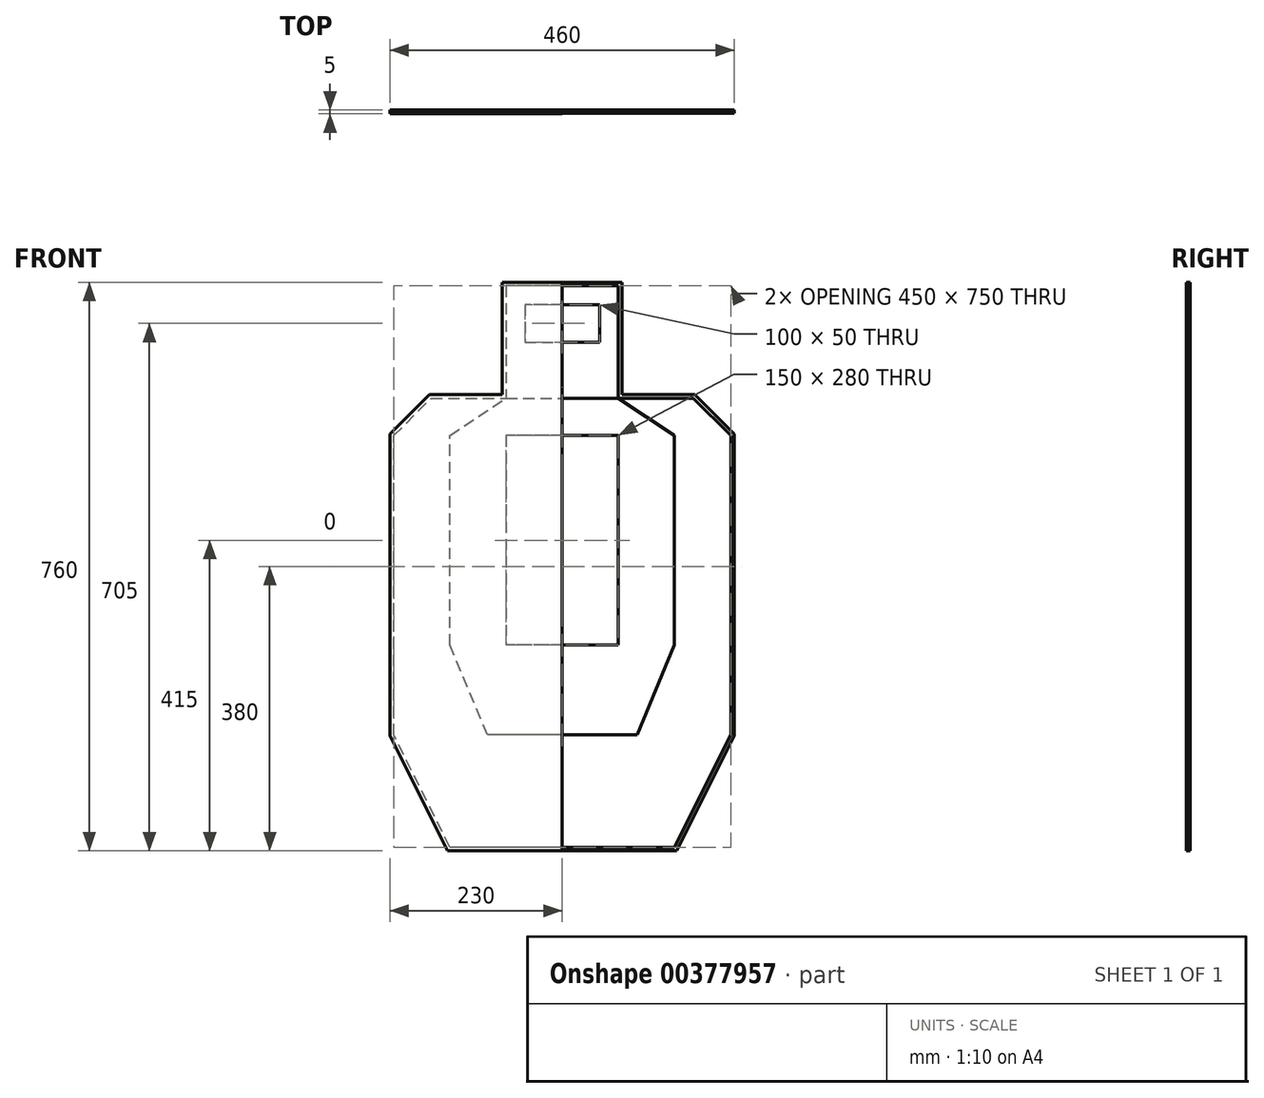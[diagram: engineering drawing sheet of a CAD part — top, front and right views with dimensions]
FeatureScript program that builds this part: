
annotation { "Feature Type Name" : "Feature", "Feature Type Description" : "" }
export const myFeature = defineFeature(function(context is Context, id is Id, definition is map)
    precondition{}
    {
        {
            var Q0;
            Q0=qCreatedBy(makeId("Front.planeOp"),FACE);
            var sketch = newSketch(context, id + "F0", { "sketchPlane" : qUnion([Q0])});
            skLineSegment(sketch, "E0.bottom", {"start": v(0, 100) * mm, "end": v(50, 100) * mm, "construction": true});
            skLineSegment(sketch, "E0.top", {"start": v(0, 125) * mm, "end": v(50, 125) * mm});
            skLineSegment(sketch, "E0.right", {"start": v(50, 100) * mm, "end": v(50, 125) * mm});
            skLineSegment(sketch, "E1.MirrorCS", {"start": v(0, 75) * mm, "end": v(50, 75) * mm});
            skLineSegment(sketch, "E2.MirrorCS", {"start": v(50, 100) * mm, "end": v(50, 75) * mm});
            skLineSegment(sketch, "E3.MirrorCS", {"start": v(0, 0) * mm, "end": v(0, 100) * mm, "construction": true});
            skLineSegment(sketch, "E4.MirrorCS", {"start": v(0, 125) * mm, "end": v(-50, 125) * mm});
            skLineSegment(sketch, "E5.MirrorCS", {"start": v(-50, 100) * mm, "end": v(-50, 125) * mm});
            skLineSegment(sketch, "E6.MirrorCS", {"start": v(-50, 100) * mm, "end": v(-50, 75) * mm});
            skLineSegment(sketch, "E7.MirrorCS", {"start": v(0, 75) * mm, "end": v(-50, 75) * mm});
            skSolve(sketch);
        }
        {
            var Q0;
            Q0=qSketchRegion(id+"F0",true);
            extrude(context, id + "F1", {"entities" : qUnion([Q0]), "oppositeDirection" : true, "depth" : 3 * mm});
        }
        {
            var Q0;
            Q0=qCreatedBy(makeId("Front.planeOp"),FACE);
            var sketch = newSketch(context, id + "F2", { "sketchPlane" : qUnion([Q0])});
            skLineSegment(sketch, "E8", {"start": v(75, 0) * mm, "end": v(75, 150) * mm});
            skLineSegment(sketch, "E9", {"start": v(75, 150) * mm, "end": v(-75, 150) * mm});
            skLineSegment(sketch, "E10", {"start": v(-75, 150) * mm, "end": v(-75, 0) * mm});
            skLineSegment(sketch, "E11", {"start": v(-75, 0) * mm, "end": v(75, 0) * mm});
            skLineSegment(sketch, "E12.0", {"start": v(0, 125) * mm, "end": v(-50, 125) * mm});
            skLineSegment(sketch, "E13.0", {"start": v(0, 125) * mm, "end": v(50, 125) * mm});
            skLineSegment(sketch, "E14.0", {"start": v(50, 100) * mm, "end": v(50, 125) * mm});
            skLineSegment(sketch, "E15.1", {"start": v(50, 100) * mm, "end": v(50, 75) * mm});
            skLineSegment(sketch, "E16.0", {"start": v(0, 75) * mm, "end": v(50, 75) * mm});
            skLineSegment(sketch, "E17.0", {"start": v(0, 75) * mm, "end": v(-50, 75) * mm});
            skLineSegment(sketch, "E18.0", {"start": v(-50, 100) * mm, "end": v(-50, 75) * mm});
            skLineSegment(sketch, "E19.1", {"start": v(-50, 100) * mm, "end": v(-50, 125) * mm});
            skLineSegment(sketch, "E20", {"start": v(0, 125) * mm, "end": v(0, 150) * mm, "construction": true});
            skLineSegment(sketch, "E21", {"start": v(0, 150) * mm, "end": v(0, 137.5) * mm, "construction": true});
            skSolve(sketch);
        }
        {
            var Q0;
            {var subQ0=sQuery(id+"F2.wireOp",EDGE,"E8");Q0=makeQuery(id+"F2.imprint","IMPRINT",FACE,{"disambiguationData":[TD([[makeQuery(id+"F2.imprint","IMPRINT",EDGE,{"derivedFrom":subQ0}),1.0]])]});}
            extrude(context, id + "F3", {"entities" : qUnion([Q0]), "oppositeDirection" : true, "depth" : 3 * mm});
        }
        {
            var Q0;
            Q0=qCreatedBy(makeId("Front.planeOp"),FACE);
            var sketch = newSketch(context, id + "F4", { "sketchPlane" : qUnion([Q0])});
            skLineSegment(sketch, "E22.bottom", {"start": v(75, -50) * mm, "end": v(-75, -50) * mm});
            skLineSegment(sketch, "E22.top", {"start": v(75, -330) * mm, "end": v(-75, -330) * mm});
            skLineSegment(sketch, "E22.left", {"start": v(75, -50) * mm, "end": v(75, -330) * mm});
            skLineSegment(sketch, "E22.right", {"start": v(-75, -50) * mm, "end": v(-75, -330) * mm});
            skLineSegment(sketch, "E23", {"start": v(0, 0) * mm, "end": v(0, -50) * mm, "construction": true});
            skLineSegment(sketch, "E24.0", {"start": v(-75, 0) * mm, "end": v(75, 0) * mm, "construction": true});
            skLineSegment(sketch, "E25", {"start": v(75, 0) * mm, "end": v(75, -50) * mm, "construction": true});
            skSolve(sketch);
        }
        {
            var Q0;
            Q0=makeQuery(id+"F4.imprint","IMPRINT",FACE,{"disambiguationData":[TD([[makeQuery(id+"F4.imprint","IMPRINT",EDGE,{"derivedFrom":sQuery(id+"F4.wireOp",EDGE,"E22.bottom")}),1.0]])]});
            extrude(context, id + "F5", {"entities" : qUnion([Q0]), "oppositeDirection" : true, "depth" : 3 * mm});
        }
        {
            var Q0;
            Q0=qCreatedBy(makeId("Front.planeOp"),FACE);
            var sketch = newSketch(context, id + "F6", { "sketchPlane" : qUnion([Q0])});
            skLineSegment(sketch, "E26.0", {"start": v(-75, 0) * mm, "end": v(75, 0) * mm});
            skLineSegment(sketch, "E27.1", {"start": v(75, -50) * mm, "end": v(75, -330) * mm});
            skLineSegment(sketch, "E28.2", {"start": v(75, -50) * mm, "end": v(-75, -50) * mm});
            skLineSegment(sketch, "E29.3", {"start": v(-75, -50) * mm, "end": v(-75, -330) * mm});
            skLineSegment(sketch, "E30.0", {"start": v(75, -330) * mm, "end": v(-75, -330) * mm});
            skLineSegment(sketch, "E31", {"start": v(75, 0) * mm, "end": v(150, -50) * mm});
            skLineSegment(sketch, "E32", {"start": v(150, -50) * mm, "end": v(150, -330) * mm});
            skLineSegment(sketch, "E33", {"start": v(150, -330) * mm, "end": v(100, -450) * mm});
            skLineSegment(sketch, "E34", {"start": v(100, -450) * mm, "end": v(-100, -450) * mm});
            skLineSegment(sketch, "E35", {"start": v(-100, -450) * mm, "end": v(-150, -330) * mm});
            skLineSegment(sketch, "E36", {"start": v(-150, -330) * mm, "end": v(-150, -50) * mm});
            skLineSegment(sketch, "E37", {"start": v(-150, -50) * mm, "end": v(-75, 0) * mm});
            skLineSegment(sketch, "E38", {"start": v(0, -450) * mm, "end": v(0, -50) * mm, "construction": true});
            skLineSegment(sketch, "E39", {"start": v(150, -50) * mm, "end": v(75, -50) * mm, "construction": true});
            skLineSegment(sketch, "E40", {"start": v(-55.04, -50) * mm, "end": v(-150, -50) * mm, "construction": true});
            skLineSegment(sketch, "E41", {"start": v(150, -330) * mm, "end": v(150, -450) * mm, "construction": true});
            skLineSegment(sketch, "E42", {"start": v(100, -450) * mm, "end": v(150, -450) * mm, "construction": true});
            skLineSegment(sketch, "E43", {"start": v(150, -330) * mm, "end": v(-150, -330) * mm, "construction": true});
            skLineSegment(sketch, "E44", {"start": v(-150, -330) * mm, "end": v(-150, -450) * mm, "construction": true});
            skLineSegment(sketch, "E45", {"start": v(-150, -450) * mm, "end": v(-100, -450) * mm, "construction": true});
            skSolve(sketch);
        }
        {
            var Q0;
            Q0=makeQuery(id+"F6.imprint","IMPRINT",FACE,{"disambiguationData":[TD([[makeQuery(id+"F6.imprint","IMPRINT",EDGE,{"derivedFrom":sQuery(id+"F6.wireOp",EDGE,"E26.0")}),-1.0]])]});
            extrude(context, id + "F7", {"entities" : qUnion([Q0]), "oppositeDirection" : true, "depth" : 3 * mm});
        }
        {
            var Q0;
            Q0=makeQuery(id+"F7.opExtrude","CAP_FACE",FACE,{"disambiguationData":[OSD([sQuery(id+"F6.wireOp",EDGE,"E26.0"),sQuery(id+"F6.wireOp",EDGE,"E27.1"),sQuery(id+"F6.wireOp",EDGE,"E28.2"),sQuery(id+"F6.wireOp",EDGE,"E29.3"),sQuery(id+"F6.wireOp",EDGE,"E30.0"),sQuery(id+"F6.wireOp",EDGE,"E31"),sQuery(id+"F6.wireOp",EDGE,"E32"),sQuery(id+"F6.wireOp",EDGE,"E33"),sQuery(id+"F6.wireOp",EDGE,"E34"),sQuery(id+"F6.wireOp",EDGE,"E35"),sQuery(id+"F6.wireOp",EDGE,"E36"),sQuery(id+"F6.wireOp",EDGE,"E37")])],"isStart":true});
            var sketch = newSketch(context, id + "F8", { "sketchPlane" : qUnion([Q0])});
            skLineSegment(sketch, "E46.0", {"start": v(75, 0) * mm, "end": v(150, -50) * mm});
            skLineSegment(sketch, "E47.0", {"start": v(150, -50) * mm, "end": v(150, -330) * mm});
            skLineSegment(sketch, "E48.0", {"start": v(150, -330) * mm, "end": v(100, -450) * mm});
            skLineSegment(sketch, "E49.1", {"start": v(100, -450) * mm, "end": v(-100, -450) * mm});
            skLineSegment(sketch, "E50.0", {"start": v(-150, -330) * mm, "end": v(-150, -50) * mm});
            skLineSegment(sketch, "E51.0", {"start": v(-100, -450) * mm, "end": v(-150, -330) * mm});
            skLineSegment(sketch, "E52.0", {"start": v(-150, -50) * mm, "end": v(-75, 0) * mm});
            skLineSegment(sketch, "E53", {"start": v(75, 0) * mm, "end": v(175, 0) * mm});
            skLineSegment(sketch, "E54", {"start": v(175, 0) * mm, "end": v(225, -50) * mm});
            skLineSegment(sketch, "E55", {"start": v(225, -50) * mm, "end": v(225, -450) * mm});
            skLineSegment(sketch, "E56", {"start": v(225, -450) * mm, "end": v(150, -600) * mm});
            skLineSegment(sketch, "E57", {"start": v(150, -600) * mm, "end": v(-150, -600) * mm});
            skLineSegment(sketch, "E58", {"start": v(-150, -600) * mm, "end": v(-225, -450) * mm});
            skLineSegment(sketch, "E59", {"start": v(-225, -450) * mm, "end": v(-225, -50) * mm});
            skLineSegment(sketch, "E60", {"start": v(-225, -50) * mm, "end": v(-175, 0) * mm});
            skLineSegment(sketch, "E61", {"start": v(-175, 0) * mm, "end": v(-75, 0) * mm});
            skLineSegment(sketch, "E62", {"start": v(225, -50) * mm, "end": v(225, 0) * mm, "construction": true});
            skLineSegment(sketch, "E63", {"start": v(225, 0) * mm, "end": v(175, 0) * mm, "construction": true});
            skLineSegment(sketch, "E64", {"start": v(225, -450) * mm, "end": v(225, -600) * mm, "construction": true});
            skLineSegment(sketch, "E65", {"start": v(225, -600) * mm, "end": v(150, -600) * mm, "construction": true});
            skLineSegment(sketch, "E66", {"start": v(-225, -450) * mm, "end": v(-225, -600) * mm, "construction": true});
            skLineSegment(sketch, "E67", {"start": v(-225, -600) * mm, "end": v(-150, -600) * mm, "construction": true});
            skLineSegment(sketch, "E68", {"start": v(-175, 0) * mm, "end": v(-225, 0) * mm, "construction": true});
            skLineSegment(sketch, "E69", {"start": v(-225, 0) * mm, "end": v(-225, -50) * mm, "construction": true});
            skSolve(sketch);
        }
        {
            var Q0;
            Q0=qSketchRegion(id+"F8",true);
            extrude(context, id + "F9", {"entities" : qUnion([Q0]), "oppositeDirection" : true, "depth" : 3 * mm});
        }
        {
            var Q0;
            Q0=makeQuery(id+"F9.opExtrude","CAP_FACE",FACE,{"disambiguationData":[OSD([sQuery(id+"F8.wireOp",EDGE,"E46.0"),sQuery(id+"F8.wireOp",EDGE,"E47.0"),sQuery(id+"F8.wireOp",EDGE,"E48.0"),sQuery(id+"F8.wireOp",EDGE,"E49.1"),sQuery(id+"F8.wireOp",EDGE,"E50.0"),sQuery(id+"F8.wireOp",EDGE,"E51.0"),sQuery(id+"F8.wireOp",EDGE,"E52.0"),sQuery(id+"F8.wireOp",EDGE,"E53"),sQuery(id+"F8.wireOp",EDGE,"E54"),sQuery(id+"F8.wireOp",EDGE,"E55"),sQuery(id+"F8.wireOp",EDGE,"E56"),sQuery(id+"F8.wireOp",EDGE,"E57"),sQuery(id+"F8.wireOp",EDGE,"E58"),sQuery(id+"F8.wireOp",EDGE,"E59"),sQuery(id+"F8.wireOp",EDGE,"E60"),sQuery(id+"F8.wireOp",EDGE,"E61")])],"isStart":true});
            var sketch = newSketch(context, id + "F10", { "sketchPlane" : qUnion([Q0])});
            skLineSegment(sketch, "E70.0", {"start": v(75, 150) * mm, "end": v(-75, 150) * mm});
            skLineSegment(sketch, "E71.0", {"start": v(75, 0) * mm, "end": v(75, 150) * mm});
            skLineSegment(sketch, "E72.1", {"start": v(75, 0) * mm, "end": v(175, 0) * mm});
            skLineSegment(sketch, "E73.0", {"start": v(175, 0) * mm, "end": v(225, -50) * mm});
            skLineSegment(sketch, "E74.1", {"start": v(225, -50) * mm, "end": v(225, -450) * mm});
            skLineSegment(sketch, "E75.0", {"start": v(225, -450) * mm, "end": v(150, -600) * mm});
            skLineSegment(sketch, "E76.1", {"start": v(150, -600) * mm, "end": v(-150, -600) * mm});
            skLineSegment(sketch, "E77.2", {"start": v(-150, -600) * mm, "end": v(-225, -450) * mm});
            skLineSegment(sketch, "E78.3", {"start": v(-225, -450) * mm, "end": v(-225, -50) * mm});
            skLineSegment(sketch, "E79.4", {"start": v(-225, -50) * mm, "end": v(-175, 0) * mm});
            skLineSegment(sketch, "E80.5", {"start": v(-175, 0) * mm, "end": v(-75, 0) * mm});
            skLineSegment(sketch, "E81.0", {"start": v(-75, 150) * mm, "end": v(-75, 0) * mm});
            skLineSegment(sketch, "E82.0", {"start": v(177.07, 5) * mm, "end": v(230, -47.93) * mm});
            skLineSegment(sketch, "E82.1", {"start": v(-230, -451.18) * mm, "end": v(-230, -47.93) * mm});
            skLineSegment(sketch, "E82.2", {"start": v(-153.1, -605) * mm, "end": v(-230, -451.18) * mm});
            skLineSegment(sketch, "E82.3", {"start": v(153.1, -605) * mm, "end": v(-153.1, -605) * mm});
            skLineSegment(sketch, "E82.4", {"start": v(230, -451.18) * mm, "end": v(153.1, -605) * mm});
            skLineSegment(sketch, "E82.5", {"start": v(-230, -47.93) * mm, "end": v(-177.07, 5) * mm});
            skLineSegment(sketch, "E82.6", {"start": v(230, -47.93) * mm, "end": v(230, -451.18) * mm});
            skLineSegment(sketch, "E82.7", {"start": v(-177.07, 5) * mm, "end": v(-80, 5) * mm});
            skLineSegment(sketch, "E82.8", {"start": v(-80, 155) * mm, "end": v(-80, 5) * mm});
            skLineSegment(sketch, "E82.9", {"start": v(80, 155) * mm, "end": v(-80, 155) * mm});
            skLineSegment(sketch, "E82.10", {"start": v(80, 5) * mm, "end": v(80, 155) * mm});
            skLineSegment(sketch, "E82.11", {"start": v(80, 5) * mm, "end": v(177.07, 5) * mm});
            skSolve(sketch);
        }
        {
            var Q0;
            Q0=makeQuery(id+"F10.imprint","IMPRINT",FACE,{"disambiguationData":[TD([[makeQuery(id+"F10.imprint","IMPRINT",EDGE,{"derivedFrom":sQuery(id+"F10.wireOp",EDGE,"E70.0")}),-1.0]])]});
            extrude(context, id + "F11", {"entities" : qUnion([Q0]), "oppositeDirection" : true, "depth" : 3 * mm});
        }
        {
            var Q0;
            Q0=makeQuery(id+"F9.opExtrude","CAP_FACE",FACE,{"disambiguationData":[OSD([sQuery(id+"F8.wireOp",EDGE,"E46.0"),sQuery(id+"F8.wireOp",EDGE,"E47.0"),sQuery(id+"F8.wireOp",EDGE,"E48.0"),sQuery(id+"F8.wireOp",EDGE,"E49.1"),sQuery(id+"F8.wireOp",EDGE,"E50.0"),sQuery(id+"F8.wireOp",EDGE,"E51.0"),sQuery(id+"F8.wireOp",EDGE,"E52.0"),sQuery(id+"F8.wireOp",EDGE,"E53"),sQuery(id+"F8.wireOp",EDGE,"E54"),sQuery(id+"F8.wireOp",EDGE,"E55"),sQuery(id+"F8.wireOp",EDGE,"E56"),sQuery(id+"F8.wireOp",EDGE,"E57"),sQuery(id+"F8.wireOp",EDGE,"E58"),sQuery(id+"F8.wireOp",EDGE,"E59"),sQuery(id+"F8.wireOp",EDGE,"E60"),sQuery(id+"F8.wireOp",EDGE,"E61")])],"isStart":false});
            var sketch = newSketch(context, id + "F12", { "sketchPlane" : qUnion([Q0])});
            skLineSegment(sketch, "E83.0", {"start": v(75, 150) * mm, "end": v(75, 0) * mm});
            skLineSegment(sketch, "E84.0", {"start": v(175, 0) * mm, "end": v(75, 0) * mm});
            skLineSegment(sketch, "E85.0", {"start": v(-75, 150) * mm, "end": v(75, 150) * mm});
            skLineSegment(sketch, "E86.0", {"start": v(225, -50) * mm, "end": v(175, 0) * mm});
            skLineSegment(sketch, "E87.0", {"start": v(-225, -50) * mm, "end": v(-225, -450) * mm});
            skLineSegment(sketch, "E87.1", {"start": v(225, -450) * mm, "end": v(225, -50) * mm});
            skLineSegment(sketch, "E87.2", {"start": v(150, -600) * mm, "end": v(225, -450) * mm});
            skLineSegment(sketch, "E87.3", {"start": v(-225, -450) * mm, "end": v(-150, -600) * mm});
            skLineSegment(sketch, "E87.4", {"start": v(-150, -600) * mm, "end": v(150, -600) * mm});
            skLineSegment(sketch, "E88.0", {"start": v(-175, 0) * mm, "end": v(-225, -50) * mm});
            skLineSegment(sketch, "E89.0", {"start": v(-75, 0) * mm, "end": v(-175, 0) * mm});
            skLineSegment(sketch, "E90.0", {"start": v(-75, 0) * mm, "end": v(-75, 150) * mm});
            skSolve(sketch);
        }
        {
            var Q0;
            Q0=qSketchRegion(id+"F12",true);
            extrude(context, id + "F13", {"entities" : qUnion([Q0]), "depth" : 1 * mm});
        }
        {
            var Q0;
            Q0=makeQuery(id+"F13.opExtrude","CAP_FACE",FACE,{"disambiguationData":[OSD([sQuery(id+"F12.wireOp",EDGE,"E83.0"),sQuery(id+"F12.wireOp",EDGE,"E84.0"),sQuery(id+"F12.wireOp",EDGE,"E85.0"),sQuery(id+"F12.wireOp",EDGE,"E86.0"),sQuery(id+"F12.wireOp",EDGE,"E87.0"),sQuery(id+"F12.wireOp",EDGE,"E87.1"),sQuery(id+"F12.wireOp",EDGE,"E87.2"),sQuery(id+"F12.wireOp",EDGE,"E87.3"),sQuery(id+"F12.wireOp",EDGE,"E87.4"),sQuery(id+"F12.wireOp",EDGE,"E88.0"),sQuery(id+"F12.wireOp",EDGE,"E89.0"),sQuery(id+"F12.wireOp",EDGE,"E90.0")])],"isStart":false});
            var sketch = newSketch(context, id + "F14", { "sketchPlane" : qUnion([Q0])});
            skLineSegment(sketch, "E91.0", {"start": v(-80, 155) * mm, "end": v(80, 155) * mm});
            skLineSegment(sketch, "E92.0", {"start": v(80, 155) * mm, "end": v(80, 5) * mm});
            skLineSegment(sketch, "E93.0", {"start": v(-80, 5) * mm, "end": v(-80, 155) * mm});
            skLineSegment(sketch, "E94.0", {"start": v(177.07, 5) * mm, "end": v(80, 5) * mm});
            skLineSegment(sketch, "E95.0", {"start": v(-80, 5) * mm, "end": v(-177.07, 5) * mm});
            skLineSegment(sketch, "E96.0", {"start": v(230, -47.93) * mm, "end": v(177.07, 5) * mm});
            skLineSegment(sketch, "E97.0", {"start": v(-177.07, 5) * mm, "end": v(-230, -47.93) * mm});
            skLineSegment(sketch, "E98.1", {"start": v(-230, -47.93) * mm, "end": v(-230, -451.18) * mm});
            skLineSegment(sketch, "E99.0", {"start": v(-230, -451.18) * mm, "end": v(-153.1, -605) * mm});
            skLineSegment(sketch, "E100.0", {"start": v(-153.1, -605) * mm, "end": v(153.1, -605) * mm});
            skLineSegment(sketch, "E101.0", {"start": v(153.1, -605) * mm, "end": v(230, -451.18) * mm});
            skLineSegment(sketch, "E102.0", {"start": v(230, -451.18) * mm, "end": v(230, -47.93) * mm});
            skLineSegment(sketch, "E103.0", {"start": v(-75, 150) * mm, "end": v(75, 150) * mm});
            skLineSegment(sketch, "E104.0", {"start": v(-75, 0) * mm, "end": v(-75, 150) * mm});
            skLineSegment(sketch, "E105.0", {"start": v(75, 150) * mm, "end": v(75, 0) * mm});
            skLineSegment(sketch, "E106.0", {"start": v(175, 0) * mm, "end": v(75, 0) * mm});
            skLineSegment(sketch, "E107.0", {"start": v(225, -50) * mm, "end": v(175, 0) * mm});
            skLineSegment(sketch, "E108.0", {"start": v(150, -600) * mm, "end": v(225, -450) * mm});
            skLineSegment(sketch, "E109.0", {"start": v(225, -450) * mm, "end": v(225, -50) * mm});
            skLineSegment(sketch, "E110.0", {"start": v(-150, -600) * mm, "end": v(150, -600) * mm});
            skLineSegment(sketch, "E111.0", {"start": v(-225, -450) * mm, "end": v(-150, -600) * mm});
            skLineSegment(sketch, "E112.0", {"start": v(-225, -50) * mm, "end": v(-225, -450) * mm});
            skLineSegment(sketch, "E113.0", {"start": v(-175, 0) * mm, "end": v(-225, -50) * mm});
            skLineSegment(sketch, "E114.0", {"start": v(-75, 0) * mm, "end": v(-175, 0) * mm});
            skSolve(sketch);
        }
        {
            var Q0;
            Q0=makeQuery(id+"F14.imprint","IMPRINT",FACE,{"disambiguationData":[TD([[makeQuery(id+"F14.imprint","IMPRINT",EDGE,{"derivedFrom":sQuery(id+"F14.wireOp",EDGE,"E91.0")}),-1.0]])]});
            extrude(context, id + "F15", {"entities" : qUnion([Q0]), "oppositeDirection" : true, "depth" : 1 * mm});
        }
        {
            var Q0;
            Q0=makeQuery(id+"F9.opExtrude","CAP_FACE",FACE,{"disambiguationData":[OSD([sQuery(id+"F8.wireOp",EDGE,"E46.0"),sQuery(id+"F8.wireOp",EDGE,"E47.0"),sQuery(id+"F8.wireOp",EDGE,"E48.0"),sQuery(id+"F8.wireOp",EDGE,"E49.1"),sQuery(id+"F8.wireOp",EDGE,"E50.0"),sQuery(id+"F8.wireOp",EDGE,"E51.0"),sQuery(id+"F8.wireOp",EDGE,"E52.0"),sQuery(id+"F8.wireOp",EDGE,"E53"),sQuery(id+"F8.wireOp",EDGE,"E54"),sQuery(id+"F8.wireOp",EDGE,"E55"),sQuery(id+"F8.wireOp",EDGE,"E56"),sQuery(id+"F8.wireOp",EDGE,"E57"),sQuery(id+"F8.wireOp",EDGE,"E58"),sQuery(id+"F8.wireOp",EDGE,"E59"),sQuery(id+"F8.wireOp",EDGE,"E60"),sQuery(id+"F8.wireOp",EDGE,"E61")])],"isStart":true});
            var sketch = newSketch(context, id + "F16", { "sketchPlane" : qUnion([Q0])});
            skLineSegment(sketch, "E115.0", {"start": v(0, -605) * mm, "end": v(-153.1, -605) * mm});
            skLineSegment(sketch, "E116.0", {"start": v(-153.1, -605) * mm, "end": v(-230, -451.18) * mm});
            skLineSegment(sketch, "E117.0", {"start": v(-230, -451.18) * mm, "end": v(-230, -47.93) * mm});
            skLineSegment(sketch, "E118.0", {"start": v(-230, -47.93) * mm, "end": v(-177.07, 5) * mm});
            skLineSegment(sketch, "E119.0", {"start": v(-177.07, 5) * mm, "end": v(-80, 5) * mm});
            skLineSegment(sketch, "E120.0", {"start": v(-80, 155) * mm, "end": v(-80, 5) * mm});
            skLineSegment(sketch, "E121.0", {"start": v(80, 155) * mm, "end": v(-80, 155) * mm});
            skLineSegment(sketch, "E122", {"start": v(0, -605) * mm, "end": v(0, 155) * mm});
            skSolve(sketch);
        }
        {
            var Q0;
            Q0=qSketchRegion(id+"F16",true);
            extrude(context, id + "F17", {"entities" : qUnion([Q0]), "depth" : 1 * mm});
        }
    });
